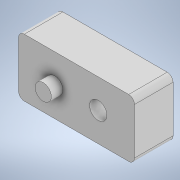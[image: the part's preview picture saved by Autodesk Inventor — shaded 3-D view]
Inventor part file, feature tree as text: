
AUTODESK INVENTOR PART (.ipt)
format: ipt  version: 2021 (Build 250183000, 183)  size: 116,224 bytes
history: native  units: mm
features: extrude x2, sketch x2, fillet x1
ambient origin geometry x8: Origin, YZ Plane, XZ Plane, XY Plane, X Axis, Y Axis, Z Axis, Center Point
bodies: Solid1 (feature_tree)
feature tree (5):
  extrude  "Extrusion1"  Depth=10.0mm
  extrude  "Extrusion2"  Depth=3.75mm
  fillet  "Fillet2"  Radius=6.65mm
  sketch  "Sketch1"  dims[d0=20.0mm d1=10.0mm]
  sketch  "Sketch2"  dims[d2=3.0mm d3=3.75mm d4=6.65mm d5=0.0mm d6=2.8mm d7=3.75mm d8=2.0mm d9=0.0mm d13=1.0mm]
